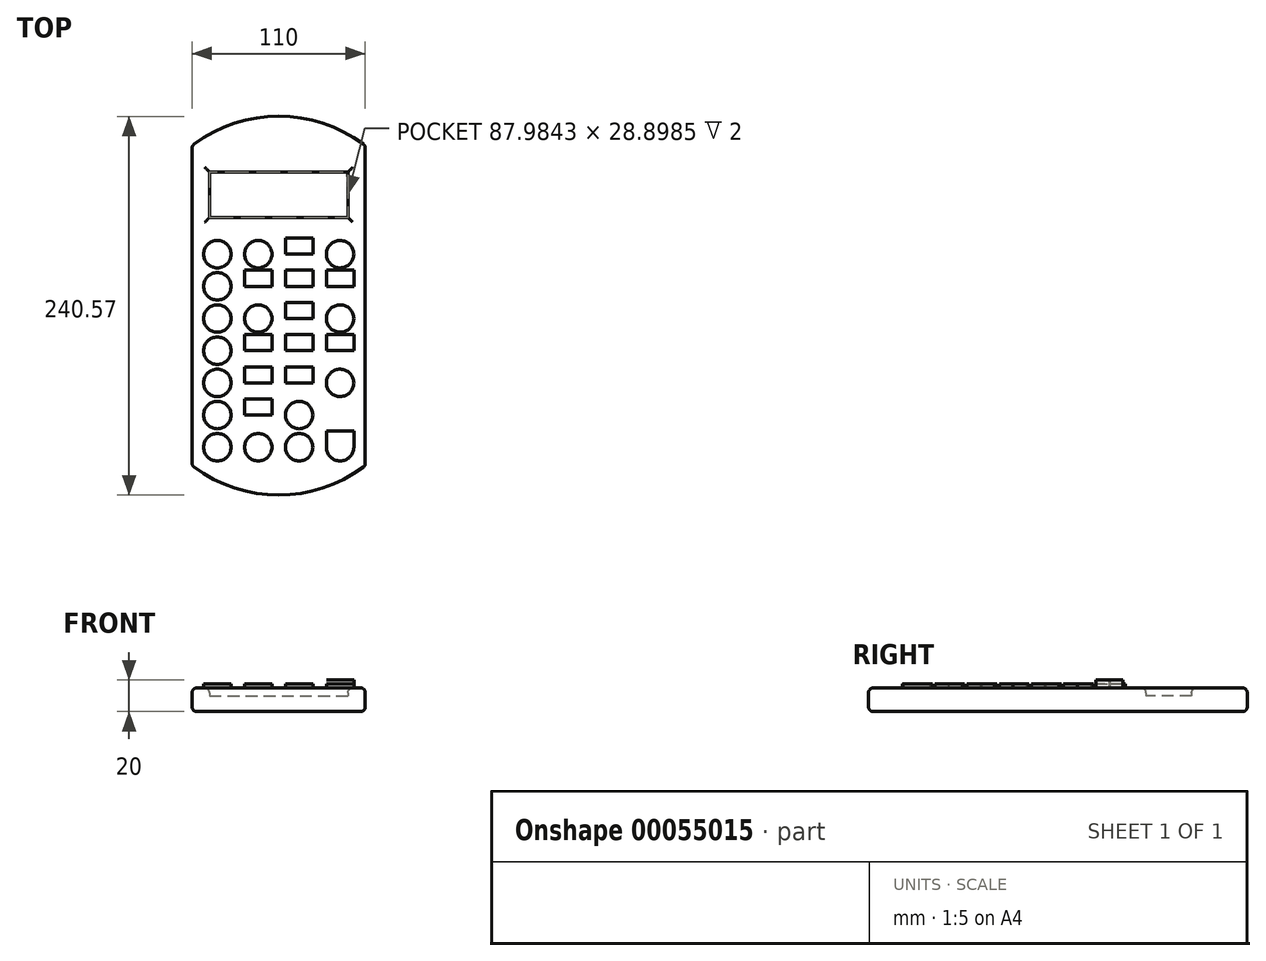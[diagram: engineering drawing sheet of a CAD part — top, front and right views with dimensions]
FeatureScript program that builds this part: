
annotation { "Feature Type Name" : "Feature", "Feature Type Description" : "" }
export const myFeature = defineFeature(function(context is Context, id is Id, definition is map)
    precondition{}
    {
        {
            var Q0;
            Q0=qCreatedBy(makeId("Top.planeOp"),FACE);
            var sketch = newSketch(context, id + "F0", { "sketchPlane" : qUnion([Q0])});
            skLineSegment(sketch, "E0.left", {"start": v(-37.1, 78.15) * mm, "end": v(-37.1, -125.06) * mm});
            skLineSegment(sketch, "E0.right", {"start": v(72.9, 78.15) * mm, "end": v(72.9, -125.06) * mm});
            skLineSegment(sketch, "E1", {"start": v(-37.1, -125.06) * mm, "end": v(72.9, -125.06) * mm});
            skPoint(sketch, "E2.endSnap0", {"position": v(17.9, -125.06) * mm});
            skArc(sketch, "E3", {"start": v(-37.1, -125.06) * mm, "mid": v(17.9, -143.74) * mm, "end": v(72.9, -125.06) * mm});
            skPoint(sketch, "E2.end.orphan", {"position": v(17.9, -16.69) * mm});
            skLineSegment(sketch, "E4", {"start": v(17.9, -125.06) * mm, "end": v(17.9, -143.74) * mm});
            skLineSegment(sketch, "E5", {"start": v(17.9, 96.83) * mm, "end": v(17.9, 78.15) * mm});
            skArc(sketch, "E6", {"start": v(72.9, 78.15) * mm, "mid": v(17.9, 96.83) * mm, "end": v(-37.1, 78.15) * mm});
            skLineSegment(sketch, "E7.rect.bottom", {"start": v(-26.1, 61.47) * mm, "end": v(61.9, 61.47) * mm});
            skLineSegment(sketch, "E7.rect.top", {"start": v(-26.1, 32.57) * mm, "end": v(61.9, 32.57) * mm});
            skLineSegment(sketch, "E7.rect.left", {"start": v(-26.1, 61.47) * mm, "end": v(-26.1, 32.57) * mm});
            skLineSegment(sketch, "E7.rect.right", {"start": v(61.9, 61.47) * mm, "end": v(61.9, 32.57) * mm});
            skPoint(sketch, "E7.rect.middle", {"position": v(17.9, 47.02) * mm});
            skPoint(sketch, "E8.orphan", {"position": v(-37.1, 96.83) * mm});
            skPoint(sketch, "E9.orphan", {"position": v(72.9, 96.83) * mm});
            skSolve(sketch);
        }
        {
            var Q0;
            {var subQ4=sQuery(id+"F0.wireOp",EDGE,"E0.left");Q0=makeQuery(id+"F0.imprint","IMPRINT",FACE,{"disambiguationData":[TD([[makeQuery(id+"F0.imprint","IMPRINT",EDGE,{"derivedFrom":subQ4}),1.0]])]});}
            var Q1;
            {var subQ3=sQuery(id+"F0.wireOp",EDGE,"E4");Q1=makeQuery(id+"F0.imprint","IMPRINT",FACE,{"disambiguationData":[TD([[makeQuery(id+"F0.imprint","IMPRINT",EDGE,{"derivedFrom":subQ3}),-1.0]])]});}
            var Q2;
            {var subQ3=sQuery(id+"F0.wireOp",EDGE,"E4");Q2=makeQuery(id+"F0.imprint","IMPRINT",FACE,{"disambiguationData":[TD([[makeQuery(id+"F0.imprint","IMPRINT",EDGE,{"derivedFrom":subQ3}),1.0]])]});}
            extrude(context, id + "F1", {"entities" : qUnion([Q0, Q1, Q2]), "depth" : 15 * mm});
        }
        {
            var Q0;
            Q0=makeQuery(id+"F0.imprint","IMPRINT",FACE,{"disambiguationData":[TD([[makeQuery(id+"F0.imprint","IMPRINT",EDGE,{"derivedFrom":sQuery(id+"F0.wireOp",EDGE,"E7.rect.bottom")}),-1.0]])]});
            extrude(context, id + "F2", {"entities" : qUnion([Q0]), "operationType" : NewBodyOperationType.ADD, "depth" : 10 * mm});
        }
        {
            var Q0;
            Q0=makeQuery(id+"F1.opExtrude","SWEPT_FACE",FACE,{"disambiguationData":[OSD([sQuery(id+"F0.wireOp",EDGE,"E3")])]});
            var Q1;
            Q1=makeQuery(id+"F1.opExtrude","SWEPT_FACE",FACE,{"disambiguationData":[OSD([sQuery(id+"F0.wireOp",EDGE,"E0.left")])]});
            var Q2;
            Q2=makeQuery(id+"F1.opExtrude","CAP_FACE",FACE,{"disambiguationData":[OSD([sQuery(id+"F0.wireOp",EDGE,"E0.left"),sQuery(id+"F0.wireOp",EDGE,"E0.right"),sQuery(id+"F0.wireOp",EDGE,"E3"),sQuery(id+"F0.wireOp",EDGE,"E6"),sQuery(id+"F0.wireOp",EDGE,"E7.rect.bottom"),sQuery(id+"F0.wireOp",EDGE,"E7.rect.top"),sQuery(id+"F0.wireOp",EDGE,"E7.rect.left"),sQuery(id+"F0.wireOp",EDGE,"E7.rect.right")])],"isStart":false});
            var Q3;
            Q3=makeQuery(id+"F1.opExtrude","SWEPT_FACE",FACE,{"disambiguationData":[OSD([sQuery(id+"F0.wireOp",EDGE,"E0.right")])]});
            var Q4;
            Q4=makeQuery(id+"F1.opExtrude","SWEPT_FACE",FACE,{"disambiguationData":[OSD([sQuery(id+"F0.wireOp",EDGE,"E6")])]});
            var Q5;
            {var subQ0=sQuery(id+"F0.wireOp",EDGE,"E7.rect.right");var subQ1=sQuery(id+"F0.wireOp",EDGE,"E7.rect.left");var subQ2=sQuery(id+"F0.wireOp",EDGE,"E7.rect.top");var subQ3=sQuery(id+"F0.wireOp",EDGE,"E7.rect.bottom");Q5=makeQuery(id+"F2.boolean.opBoolean","MERGE",FACE,{"derivedFrom":[makeQuery(id+"F1.opExtrude","CAP_FACE",FACE,{"disambiguationData":[OSD([sQuery(id+"F0.wireOp",EDGE,"E0.left"),sQuery(id+"F0.wireOp",EDGE,"E0.right"),sQuery(id+"F0.wireOp",EDGE,"E3"),sQuery(id+"F0.wireOp",EDGE,"E6"),subQ3,subQ2,subQ1,subQ0])],"isStart":true}),makeQuery(id+"F2.opExtrude","CAP_FACE",FACE,{"disambiguationData":[OSD([subQ3,subQ2,subQ1,subQ0])],"isStart":true})]});}
            fillet(context, id + "F3", {"entities" : qUnion([Q0, Q1, Q2, Q3, Q4, Q5]), "radius" : 3 * mm, "tangentPropagation" : true, "allowEdgeOverflow" : false});
        }
        {
            var Q0;
            Q0=makeQuery(id+"F1.opExtrude","CAP_FACE",FACE,{"disambiguationData":[OSD([sQuery(id+"F0.wireOp",EDGE,"E0.left"),sQuery(id+"F0.wireOp",EDGE,"E0.right"),sQuery(id+"F0.wireOp",EDGE,"E3"),sQuery(id+"F0.wireOp",EDGE,"E6"),sQuery(id+"F0.wireOp",EDGE,"E7.rect.bottom"),sQuery(id+"F0.wireOp",EDGE,"E7.rect.top"),sQuery(id+"F0.wireOp",EDGE,"E7.rect.left"),sQuery(id+"F0.wireOp",EDGE,"E7.rect.right")])],"isStart":false});
            var sketch = newSketch(context, id + "F4", { "sketchPlane" : qUnion([Q0])});
            skLineSegment(sketch, "E10", {"start": v(69.9, -103.13) * mm, "end": v(-34.1, -103.13) * mm});
            skLineSegment(sketch, "E11", {"start": v(69.9, -103.13) * mm, "end": v(17.9, -103.13) * mm});
            skLineSegment(sketch, "E12", {"start": v(17.9, -103.13) * mm, "end": v(43.9, -103.13) * mm});
            skLineSegment(sketch, "E13", {"start": v(43.9, -136.78) * mm, "end": v(43.9, 29.57) * mm});
            skLineSegment(sketch, "E14", {"start": v(17.9, 29.57) * mm, "end": v(17.9, -140.74) * mm});
            skLineSegment(sketch, "E15", {"start": v(17.9, -103.13) * mm, "end": v(-34.1, -103.13) * mm});
            skLineSegment(sketch, "E16", {"start": v(-8.1, -103.13) * mm, "end": v(-34.1, -103.13) * mm});
            skLineSegment(sketch, "E17", {"start": v(-8.1, -136.78) * mm, "end": v(-8.1, 29.57) * mm});
            skLineSegment(sketch, "E18", {"start": v(-34.1, -123.57) * mm, "end": v(69.9, -123.57) * mm});
            skLineSegment(sketch, "E19", {"start": v(-8.36, 29.57) * mm, "end": v(-8.36, 19.49) * mm});
            skPoint(sketch, "E20.start.orphan", {"position": v(-53.34, -40.82) * mm});
            skPoint(sketch, "E21.orphan", {"position": v(-79.34, -7.17) * mm});
            skPoint(sketch, "E22.end.orphan", {"position": v(-53.34, -7.17) * mm});
            skPoint(sketch, "E23.orphan", {"position": v(-27.34, -7.17) * mm});
            skPoint(sketch, "E24.start.orphan", {"position": v(-1.34, -40.82) * mm});
            skPoint(sketch, "E25.start.orphan", {"position": v(24.66, -7.17) * mm});
            skPoint(sketch, "E26.end.orphan", {"position": v(-1.34, -7.17) * mm});
            skLineSegment(sketch, "E27", {"start": v(-34.1, 19.49) * mm, "end": v(69.9, 19.49) * mm});
            skLineSegment(sketch, "E28", {"start": v(-34.1, -82.7) * mm, "end": v(69.9, -82.7) * mm});
            skLineSegment(sketch, "E29", {"start": v(-34.1, -62.26) * mm, "end": v(69.9, -62.26) * mm});
            skLineSegment(sketch, "E30", {"start": v(-34.1, -41.82) * mm, "end": v(69.9, -41.82) * mm});
            skLineSegment(sketch, "E31", {"start": v(-34.1, -21.38) * mm, "end": v(69.9, -21.38) * mm});
            skLineSegment(sketch, "E32", {"start": v(-34.1, -0.95) * mm, "end": v(69.9, -0.95) * mm});
            skLineSegment(sketch, "E33.bottom", {"start": v(65.6, -113.35) * mm, "end": v(48.2, -113.35) * mm});
            skLineSegment(sketch, "E33.top", {"start": v(65.6, -84.18) * mm, "end": v(48.2, -84.18) * mm});
            skLineSegment(sketch, "E33.left", {"start": v(65.6, -113.35) * mm, "end": v(65.6, -84.18) * mm});
            skLineSegment(sketch, "E33.right", {"start": v(48.2, -113.35) * mm, "end": v(48.2, -84.18) * mm});
            skLineSegment(sketch, "E34", {"start": v(48.2, -84.18) * mm, "end": v(48.2, -103.13) * mm});
            skLineSegment(sketch, "E35", {"start": v(48.2, -103.13) * mm, "end": v(48.2, -93.66) * mm});
            skArc(sketch, "E36", {"start": v(65.6, -93.66) * mm, "mid": v(56.9, -84.18) * mm, "end": v(48.2, -93.66) * mm});
            skLineSegment(sketch, "E37", {"start": v(43.9, -82.7) * mm, "end": v(43.9, -103.13) * mm});
            skLineSegment(sketch, "E38", {"start": v(43.9, -92.91) * mm, "end": v(56.9, -92.91) * mm});
            skLineSegment(sketch, "E39", {"start": v(43.9, -103.13) * mm, "end": v(43.9, -123.57) * mm});
            skLineSegment(sketch, "E40", {"start": v(43.9, -123.57) * mm, "end": v(43.9, -113.35) * mm});
            skLineSegment(sketch, "E41", {"start": v(43.9, -113.35) * mm, "end": v(56.9, -113.35) * mm});
            skPoint(sketch, "E41.endSnap0", {"position": v(56.9, -113.35) * mm});
            skArc(sketch, "E42", {"start": v(48.2, -113.35) * mm, "mid": v(56.9, -122.04) * mm, "end": v(65.6, -113.35) * mm});
            skLineSegment(sketch, "E43", {"start": v(43.9, -62.26) * mm, "end": v(43.9, -82.7) * mm});
            skLineSegment(sketch, "E44", {"start": v(43.9, -72.47) * mm, "end": v(69.9, -72.47) * mm});
            skLineSegment(sketch, "E45", {"start": v(65.6, -84.18) * mm, "end": v(65.6, -62.26) * mm});
            skLineSegment(sketch, "E46", {"start": v(48.2, -84.18) * mm, "end": v(48.2, -62.26) * mm});
            skCircle(sketch, "E47", {"center": v(56.9, -72.47) * mm, "radius": 8.7 * mm});
            skLineSegment(sketch, "E48", {"start": v(48.2, -62.26) * mm, "end": v(48.2, 19.49) * mm});
            skLineSegment(sketch, "E49", {"start": v(65.6, -62.26) * mm, "end": v(65.6, 19.49) * mm});
            skLineSegment(sketch, "E50", {"start": v(43.9, -62.26) * mm, "end": v(43.9, -41.82) * mm});
            skLineSegment(sketch, "E51", {"start": v(43.9, -41.82) * mm, "end": v(43.9, -52.04) * mm});
            skLineSegment(sketch, "E52", {"start": v(43.9, -52.04) * mm, "end": v(69.9, -52.04) * mm});
            skLineSegment(sketch, "E53", {"start": v(43.9, -21.38) * mm, "end": v(43.9, -41.82) * mm});
            skLineSegment(sketch, "E54", {"start": v(43.9, -31.6) * mm, "end": v(69.9, -31.6) * mm});
            skLineSegment(sketch, "E55", {"start": v(43.9, -0.95) * mm, "end": v(43.9, -21.38) * mm});
            skLineSegment(sketch, "E56", {"start": v(43.9, -11.16) * mm, "end": v(69.9, -11.16) * mm});
            skLineSegment(sketch, "E57", {"start": v(43.9, -0.95) * mm, "end": v(43.9, 19.49) * mm});
            skLineSegment(sketch, "E58", {"start": v(43.9, 19.49) * mm, "end": v(43.9, 9.27) * mm});
            skLineSegment(sketch, "E59", {"start": v(43.9, 9.27) * mm, "end": v(69.9, 9.27) * mm});
            skCircle(sketch, "E60", {"center": v(56.9, 9.27) * mm, "radius": 8.7 * mm});
            skCircle(sketch, "E61", {"center": v(56.9, -11.16) * mm, "radius": 8.7 * mm});
            skCircle(sketch, "E62", {"center": v(56.9, -31.6) * mm, "radius": 8.7 * mm});
            skCircle(sketch, "E63", {"center": v(56.9, -52.04) * mm, "radius": 8.7 * mm});
            skLineSegment(sketch, "E64", {"start": v(22.2, -123.57) * mm, "end": v(22.2, 19.49) * mm});
            skLineSegment(sketch, "E65", {"start": v(39.6, -123.57) * mm, "end": v(39.6, 19.49) * mm});
            skLineSegment(sketch, "E66", {"start": v(17.9, -103.13) * mm, "end": v(17.9, -123.57) * mm});
            skLineSegment(sketch, "E67", {"start": v(17.9, -123.57) * mm, "end": v(17.9, -113.35) * mm});
            skLineSegment(sketch, "E68", {"start": v(17.9, -103.13) * mm, "end": v(17.9, -82.7) * mm});
            skLineSegment(sketch, "E69", {"start": v(17.9, -113.35) * mm, "end": v(43.9, -113.35) * mm});
            skCircle(sketch, "E70", {"center": v(30.9, -113.35) * mm, "radius": 8.7 * mm});
            skLineSegment(sketch, "E71", {"start": v(30.9, -113.35) * mm, "end": v(30.9, 19.49) * mm});
            skLineSegment(sketch, "E72", {"start": v(-8.1, -103.13) * mm, "end": v(-8.1, -123.57) * mm});
            skLineSegment(sketch, "E73", {"start": v(-8.1, -123.57) * mm, "end": v(-8.1, -113.35) * mm});
            skLineSegment(sketch, "E74", {"start": v(-8.1, -113.35) * mm, "end": v(17.9, -113.35) * mm});
            skLineSegment(sketch, "E75", {"start": v(-34.1, -113.35) * mm, "end": v(-8.1, -113.35) * mm});
            skLineSegment(sketch, "E76", {"start": v(4.9, -123.57) * mm, "end": v(4.9, 19.49) * mm});
            skPoint(sketch, "E76.startSnap0", {"position": v(4.9, -113.35) * mm});
            skLineSegment(sketch, "E77", {"start": v(43.9, 9.27) * mm, "end": v(-34.1, 9.27) * mm});
            skLineSegment(sketch, "E78", {"start": v(43.9, -11.16) * mm, "end": v(-34.1, -11.16) * mm});
            skLineSegment(sketch, "E79", {"start": v(43.9, -31.6) * mm, "end": v(-34.1, -31.6) * mm});
            skLineSegment(sketch, "E80", {"start": v(43.9, -52.04) * mm, "end": v(-34.1, -52.04) * mm});
            skLineSegment(sketch, "E81", {"start": v(43.9, -72.47) * mm, "end": v(-34.1, -72.47) * mm});
            skLineSegment(sketch, "E82", {"start": v(43.9, -92.91) * mm, "end": v(-34.1, -92.91) * mm});
            skLineSegment(sketch, "E83", {"start": v(-21.1, -113.35) * mm, "end": v(-21.1, 19.49) * mm});
            skCircle(sketch, "E84", {"center": v(30.9, -92.91) * mm, "radius": 8.7 * mm});
            skCircle(sketch, "E85", {"center": v(30.9, -72.47) * mm, "radius": 8.7 * mm});
            skCircle(sketch, "E86", {"center": v(30.9, -52.04) * mm, "radius": 8.7 * mm});
            skCircle(sketch, "E87", {"center": v(30.9, -31.6) * mm, "radius": 8.7 * mm});
            skCircle(sketch, "E88", {"center": v(30.9, -11.16) * mm, "radius": 8.7 * mm});
            skCircle(sketch, "E89", {"center": v(30.9, 9.27) * mm, "radius": 8.7 * mm});
            skLineSegment(sketch, "E90", {"start": v(-8.1, 14.54) * mm, "end": v(-3.8, 14.54) * mm});
            skLineSegment(sketch, "E91", {"start": v(17.9, 14.54) * mm, "end": v(13.6, 14.54) * mm});
            skLineSegment(sketch, "E92", {"start": v(-34.1, 15.12) * mm, "end": v(-29.8, 15.12) * mm});
            skLineSegment(sketch, "E93", {"start": v(-8.1, 14.54) * mm, "end": v(-12.4, 14.54) * mm});
            skLineSegment(sketch, "E94", {"start": v(-29.8, 19.49) * mm, "end": v(-29.8, -113.35) * mm});
            skLineSegment(sketch, "E95", {"start": v(-12.4, 14.54) * mm, "end": v(-12.4, 19.49) * mm});
            skLineSegment(sketch, "E96", {"start": v(-12.4, 19.49) * mm, "end": v(-12.4, -113.35) * mm});
            skLineSegment(sketch, "E97", {"start": v(-3.8, 19.49) * mm, "end": v(-3.8, -113.35) * mm});
            skLineSegment(sketch, "E98", {"start": v(13.6, 19.49) * mm, "end": v(13.6, -113.35) * mm});
            skCircle(sketch, "E99", {"center": v(4.9, 9.27) * mm, "radius": 8.7 * mm});
            skCircle(sketch, "E100", {"center": v(4.9, -11.16) * mm, "radius": 8.7 * mm});
            skCircle(sketch, "E101", {"center": v(4.9, -31.6) * mm, "radius": 8.7 * mm});
            skCircle(sketch, "E102", {"center": v(4.9, -52.04) * mm, "radius": 8.7 * mm});
            skCircle(sketch, "E103", {"center": v(4.9, -72.47) * mm, "radius": 8.7 * mm});
            skCircle(sketch, "E104", {"center": v(4.9, -92.91) * mm, "radius": 8.7 * mm});
            skCircle(sketch, "E105", {"center": v(4.9, -113.35) * mm, "radius": 8.7 * mm});
            skCircle(sketch, "E106", {"center": v(-21.1, -113.35) * mm, "radius": 8.7 * mm});
            skCircle(sketch, "E107", {"center": v(-21.1, -92.91) * mm, "radius": 8.7 * mm});
            skCircle(sketch, "E108", {"center": v(-21.1, -72.47) * mm, "radius": 8.7 * mm});
            skCircle(sketch, "E109", {"center": v(-21.1, -52.04) * mm, "radius": 8.7 * mm});
            skCircle(sketch, "E110", {"center": v(-21.1, -31.6) * mm, "radius": 8.7 * mm});
            skCircle(sketch, "E111", {"center": v(-21.1, -11.16) * mm, "radius": 8.7 * mm});
            skCircle(sketch, "E112", {"center": v(-21.1, 9.27) * mm, "radius": 8.7 * mm});
            skSolve(sketch);
        }
        {
            var Q0;
            {var subQ7=sQuery(id+"F4.wireOp",EDGE,"E35");Q0=makeQuery(id+"F4.imprint","IMPRINT",FACE,{"disambiguationData":[TD([[makeQuery(id+"F4.imprint","IMPRINT",EDGE,{"derivedFrom":subQ7}),-1.0]])]});}
            var Q1;
            {var subQ3=sQuery(id+"F4.wireOp",EDGE,"E33.bottom");Q1=makeQuery(id+"F4.imprint","IMPRINT",FACE,{"disambiguationData":[TD([[makeQuery(id+"F4.imprint","IMPRINT",EDGE,{"derivedFrom":subQ3}),-1.0]])]});}
            var Q2;
            {var subQ0=sQuery(id+"F4.wireOp",EDGE,"E33.bottom");Q2=makeQuery(id+"F4.imprint","IMPRINT",FACE,{"disambiguationData":[TD([[makeQuery(id+"F4.imprint","IMPRINT",EDGE,{"derivedFrom":subQ0}),1.0]])]});}
            extrude(context, id + "F5", {"entities" : qUnion([Q0, Q1, Q2]), "operationType" : NewBodyOperationType.ADD, "depth" : 2.5 * mm});
        }
        {
            var Q0;
            {var subQ0=sQuery(id+"F4.wireOp",EDGE,"E46");var subQ1=sQuery(id+"F4.wireOp",EDGE,"E44");var subQ2=makeQuery(id+"F4.imprint","INTERSECT",VERTEX,{"derivedFrom":[subQ1,subQ0]});Q0=makeQuery(id+"F4.imprint","IMPRINT",FACE,{"disambiguationData":[TD([[makeQuery(id+"F4.imprint","IMPRINT",EDGE,{"disambiguationData":[TD([[subQ2,-1.0]])],"derivedFrom":subQ0}),-1.0]])]});}
            var Q1;
            {var subQ0=sQuery(id+"F4.wireOp",EDGE,"E46");var subQ1=sQuery(id+"F4.wireOp",EDGE,"E44");var subQ2=makeQuery(id+"F4.imprint","INTERSECT",VERTEX,{"derivedFrom":[subQ1,subQ0]});Q1=makeQuery(id+"F4.imprint","IMPRINT",FACE,{"disambiguationData":[TD([[makeQuery(id+"F4.imprint","IMPRINT",EDGE,{"disambiguationData":[TD([[subQ2,1.0]])],"derivedFrom":subQ0}),-1.0]])]});}
            extrude(context, id + "F6", {"entities" : qUnion([Q0, Q1]), "operationType" : NewBodyOperationType.ADD, "depth" : 2.5 * mm});
        }
        {
            var Q0;
            {var subQ0=sQuery(id+"F4.wireOp",EDGE,"E59");var subQ1=sQuery(id+"F4.wireOp",EDGE,"E48");var subQ2=makeQuery(id+"F4.imprint","INTERSECT",VERTEX,{"derivedFrom":[subQ1,subQ0]});Q0=makeQuery(id+"F4.imprint","IMPRINT",FACE,{"disambiguationData":[TD([[makeQuery(id+"F4.imprint","IMPRINT",EDGE,{"disambiguationData":[TD([[subQ2,-1.0]])],"derivedFrom":subQ1}),-1.0]])]});}
            var Q1;
            {var subQ0=sQuery(id+"F4.wireOp",EDGE,"E60");var subQ1=sQuery(id+"F4.wireOp",EDGE,"E48");var subQ2=makeQuery(id+"F4.imprint","INTERSECT",VERTEX,{"disambiguationData":[OD(0.0)],"derivedFrom":[subQ1,subQ0]});Q1=makeQuery(id+"F4.imprint","IMPRINT",FACE,{"disambiguationData":[TD([[makeQuery(id+"F4.imprint","IMPRINT",EDGE,{"disambiguationData":[TD([[subQ2,-1.0]])],"derivedFrom":subQ1}),-1.0]])]});}
            var Q2;
            {var subQ0=sQuery(id+"F4.wireOp",EDGE,"E56");var subQ1=sQuery(id+"F4.wireOp",EDGE,"E48");var subQ2=makeQuery(id+"F4.imprint","INTERSECT",VERTEX,{"derivedFrom":[subQ1,subQ0]});Q2=makeQuery(id+"F4.imprint","IMPRINT",FACE,{"disambiguationData":[TD([[makeQuery(id+"F4.imprint","IMPRINT",EDGE,{"disambiguationData":[TD([[subQ2,-1.0]])],"derivedFrom":subQ1}),-1.0]])]});}
            var Q3;
            {var subQ0=sQuery(id+"F4.wireOp",EDGE,"E61");var subQ1=sQuery(id+"F4.wireOp",EDGE,"E48");var subQ2=makeQuery(id+"F4.imprint","INTERSECT",VERTEX,{"disambiguationData":[OD(0.0)],"derivedFrom":[subQ1,subQ0]});Q3=makeQuery(id+"F4.imprint","IMPRINT",FACE,{"disambiguationData":[TD([[makeQuery(id+"F4.imprint","IMPRINT",EDGE,{"disambiguationData":[TD([[subQ2,-1.0]])],"derivedFrom":subQ1}),-1.0]])]});}
            var Q4;
            {var subQ0=sQuery(id+"F4.wireOp",EDGE,"E54");var subQ1=sQuery(id+"F4.wireOp",EDGE,"E48");var subQ2=makeQuery(id+"F4.imprint","INTERSECT",VERTEX,{"derivedFrom":[subQ1,subQ0]});Q4=makeQuery(id+"F4.imprint","IMPRINT",FACE,{"disambiguationData":[TD([[makeQuery(id+"F4.imprint","IMPRINT",EDGE,{"disambiguationData":[TD([[subQ2,-1.0]])],"derivedFrom":subQ1}),-1.0]])]});}
            var Q5;
            {var subQ0=sQuery(id+"F4.wireOp",EDGE,"E62");var subQ1=sQuery(id+"F4.wireOp",EDGE,"E48");var subQ2=makeQuery(id+"F4.imprint","INTERSECT",VERTEX,{"disambiguationData":[OD(0.0)],"derivedFrom":[subQ1,subQ0]});Q5=makeQuery(id+"F4.imprint","IMPRINT",FACE,{"disambiguationData":[TD([[makeQuery(id+"F4.imprint","IMPRINT",EDGE,{"disambiguationData":[TD([[subQ2,-1.0]])],"derivedFrom":subQ1}),-1.0]])]});}
            var Q6;
            {var subQ0=sQuery(id+"F4.wireOp",EDGE,"E52");var subQ1=sQuery(id+"F4.wireOp",EDGE,"E48");var subQ2=makeQuery(id+"F4.imprint","INTERSECT",VERTEX,{"derivedFrom":[subQ1,subQ0]});Q6=makeQuery(id+"F4.imprint","IMPRINT",FACE,{"disambiguationData":[TD([[makeQuery(id+"F4.imprint","IMPRINT",EDGE,{"disambiguationData":[TD([[subQ2,-1.0]])],"derivedFrom":subQ1}),-1.0]])]});}
            var Q7;
            {var subQ0=sQuery(id+"F4.wireOp",EDGE,"E63");var subQ1=sQuery(id+"F4.wireOp",EDGE,"E48");var subQ2=makeQuery(id+"F4.imprint","INTERSECT",VERTEX,{"disambiguationData":[OD(0.0)],"derivedFrom":[subQ1,subQ0]});Q7=makeQuery(id+"F4.imprint","IMPRINT",FACE,{"disambiguationData":[TD([[makeQuery(id+"F4.imprint","IMPRINT",EDGE,{"disambiguationData":[TD([[subQ2,-1.0]])],"derivedFrom":subQ1}),-1.0]])]});}
            extrude(context, id + "F7", {"entities" : qUnion([Q0, Q1, Q2, Q3, Q4, Q5, Q6, Q7]), "operationType" : NewBodyOperationType.ADD, "depth" : 2.5 * mm});
        }
        {
            var Q0;
            {var subQ0=sQuery(id+"F4.wireOp",EDGE,"E70");var subQ1=sQuery(id+"F4.wireOp",EDGE,"E69");var subQ2=makeQuery(id+"F4.imprint","INTERSECT",VERTEX,{"derivedFrom":[sQuery(id+"F4.wireOp",EDGE,"E64"),subQ1,subQ0]});Q0=makeQuery(id+"F4.imprint","IMPRINT",FACE,{"disambiguationData":[TD([[makeQuery(id+"F4.imprint","IMPRINT",EDGE,{"disambiguationData":[TD([[subQ2,-1.0]])],"derivedFrom":subQ1}),1.0]])]});}
            var Q1;
            {var subQ0=sQuery(id+"F4.wireOp",EDGE,"E70");var subQ1=sQuery(id+"F4.wireOp",EDGE,"E69");var subQ2=makeQuery(id+"F4.imprint","INTERSECT",VERTEX,{"derivedFrom":[sQuery(id+"F4.wireOp",EDGE,"E64"),subQ1,subQ0]});Q1=makeQuery(id+"F4.imprint","IMPRINT",FACE,{"disambiguationData":[TD([[makeQuery(id+"F4.imprint","IMPRINT",EDGE,{"disambiguationData":[TD([[subQ2,-1.0]])],"derivedFrom":subQ1}),-1.0]])]});}
            extrude(context, id + "F8", {"entities" : qUnion([Q0, Q1]), "operationType" : NewBodyOperationType.ADD, "depth" : 2.5 * mm});
        }
        {
            var Q0;
            {var subQ0=sQuery(id+"F4.wireOp",EDGE,"E71");var subQ1=sQuery(id+"F4.wireOp",EDGE,"E69");var subQ2=makeQuery(id+"F4.imprint","INTERSECT",VERTEX,{"derivedFrom":[subQ1,subQ0]});Q0=makeQuery(id+"F4.imprint","IMPRINT",FACE,{"disambiguationData":[TD([[makeQuery(id+"F4.imprint","IMPRINT",EDGE,{"disambiguationData":[TD([[subQ2,-1.0]])],"derivedFrom":subQ0}),-1.0]])]});}
            extrude(context, id + "F9", {"entities" : qUnion([Q0]), "operationType" : NewBodyOperationType.ADD, "depth" : 2.5 * mm});
        }
        {
            var Q0;
            {var subQ0=sQuery(id+"F4.wireOp",EDGE,"E84");var subQ1=sQuery(id+"F4.wireOp",EDGE,"E71");var subQ2=makeQuery(id+"F4.imprint","INTERSECT",VERTEX,{"disambiguationData":[OD(0.0)],"derivedFrom":[subQ1,subQ0]});Q0=makeQuery(id+"F4.imprint","IMPRINT",FACE,{"disambiguationData":[TD([[makeQuery(id+"F4.imprint","IMPRINT",EDGE,{"disambiguationData":[TD([[subQ2,-1.0]])],"derivedFrom":subQ1}),-1.0]])]});}
            var Q1;
            {var subQ0=sQuery(id+"F4.wireOp",EDGE,"E84");var subQ1=sQuery(id+"F4.wireOp",EDGE,"E71");var subQ2=makeQuery(id+"F4.imprint","INTERSECT",VERTEX,{"disambiguationData":[OD(0.0)],"derivedFrom":[subQ1,subQ0]});Q1=makeQuery(id+"F4.imprint","IMPRINT",FACE,{"disambiguationData":[TD([[makeQuery(id+"F4.imprint","IMPRINT",EDGE,{"disambiguationData":[TD([[subQ2,-1.0]])],"derivedFrom":subQ1}),1.0]])]});}
            var Q2;
            {var subQ0=sQuery(id+"F4.wireOp",EDGE,"E82");var subQ1=sQuery(id+"F4.wireOp",EDGE,"E71");var subQ2=makeQuery(id+"F4.imprint","INTERSECT",VERTEX,{"derivedFrom":[subQ1,subQ0]});Q2=makeQuery(id+"F4.imprint","IMPRINT",FACE,{"disambiguationData":[TD([[makeQuery(id+"F4.imprint","IMPRINT",EDGE,{"disambiguationData":[TD([[subQ2,-1.0]])],"derivedFrom":subQ1}),1.0]])]});}
            var Q3;
            {var subQ0=sQuery(id+"F4.wireOp",EDGE,"E82");var subQ1=sQuery(id+"F4.wireOp",EDGE,"E71");var subQ2=makeQuery(id+"F4.imprint","INTERSECT",VERTEX,{"derivedFrom":[subQ1,subQ0]});Q3=makeQuery(id+"F4.imprint","IMPRINT",FACE,{"disambiguationData":[TD([[makeQuery(id+"F4.imprint","IMPRINT",EDGE,{"disambiguationData":[TD([[subQ2,-1.0]])],"derivedFrom":subQ1}),-1.0]])]});}
            var Q4;
            {var subQ0=sQuery(id+"F4.wireOp",EDGE,"E85");var subQ1=sQuery(id+"F4.wireOp",EDGE,"E71");var subQ2=makeQuery(id+"F4.imprint","INTERSECT",VERTEX,{"disambiguationData":[OD(0.0)],"derivedFrom":[subQ1,subQ0]});Q4=makeQuery(id+"F4.imprint","IMPRINT",FACE,{"disambiguationData":[TD([[makeQuery(id+"F4.imprint","IMPRINT",EDGE,{"disambiguationData":[TD([[subQ2,-1.0]])],"derivedFrom":subQ1}),-1.0]])]});}
            var Q5;
            {var subQ0=sQuery(id+"F4.wireOp",EDGE,"E85");var subQ1=sQuery(id+"F4.wireOp",EDGE,"E71");var subQ2=makeQuery(id+"F4.imprint","INTERSECT",VERTEX,{"disambiguationData":[OD(0.0)],"derivedFrom":[subQ1,subQ0]});Q5=makeQuery(id+"F4.imprint","IMPRINT",FACE,{"disambiguationData":[TD([[makeQuery(id+"F4.imprint","IMPRINT",EDGE,{"disambiguationData":[TD([[subQ2,-1.0]])],"derivedFrom":subQ1}),1.0]])]});}
            var Q6;
            {var subQ0=sQuery(id+"F4.wireOp",EDGE,"E81");var subQ1=sQuery(id+"F4.wireOp",EDGE,"E71");var subQ2=makeQuery(id+"F4.imprint","INTERSECT",VERTEX,{"derivedFrom":[subQ1,subQ0]});Q6=makeQuery(id+"F4.imprint","IMPRINT",FACE,{"disambiguationData":[TD([[makeQuery(id+"F4.imprint","IMPRINT",EDGE,{"disambiguationData":[TD([[subQ2,-1.0]])],"derivedFrom":subQ1}),1.0]])]});}
            var Q7;
            {var subQ0=sQuery(id+"F4.wireOp",EDGE,"E81");var subQ1=sQuery(id+"F4.wireOp",EDGE,"E71");var subQ2=makeQuery(id+"F4.imprint","INTERSECT",VERTEX,{"derivedFrom":[subQ1,subQ0]});Q7=makeQuery(id+"F4.imprint","IMPRINT",FACE,{"disambiguationData":[TD([[makeQuery(id+"F4.imprint","IMPRINT",EDGE,{"disambiguationData":[TD([[subQ2,-1.0]])],"derivedFrom":subQ1}),-1.0]])]});}
            var Q8;
            {var subQ0=sQuery(id+"F4.wireOp",EDGE,"E80");var subQ1=sQuery(id+"F4.wireOp",EDGE,"E71");var subQ2=makeQuery(id+"F4.imprint","INTERSECT",VERTEX,{"derivedFrom":[subQ1,subQ0]});Q8=makeQuery(id+"F4.imprint","IMPRINT",FACE,{"disambiguationData":[TD([[makeQuery(id+"F4.imprint","IMPRINT",EDGE,{"disambiguationData":[TD([[subQ2,-1.0]])],"derivedFrom":subQ1}),1.0]])]});}
            var Q9;
            {var subQ0=sQuery(id+"F4.wireOp",EDGE,"E80");var subQ1=sQuery(id+"F4.wireOp",EDGE,"E71");var subQ2=makeQuery(id+"F4.imprint","INTERSECT",VERTEX,{"derivedFrom":[subQ1,subQ0]});Q9=makeQuery(id+"F4.imprint","IMPRINT",FACE,{"disambiguationData":[TD([[makeQuery(id+"F4.imprint","IMPRINT",EDGE,{"disambiguationData":[TD([[subQ2,-1.0]])],"derivedFrom":subQ1}),-1.0]])]});}
            var Q10;
            {var subQ0=sQuery(id+"F4.wireOp",EDGE,"E86");var subQ1=sQuery(id+"F4.wireOp",EDGE,"E71");var subQ2=makeQuery(id+"F4.imprint","INTERSECT",VERTEX,{"disambiguationData":[OD(0.0)],"derivedFrom":[subQ1,subQ0]});Q10=makeQuery(id+"F4.imprint","IMPRINT",FACE,{"disambiguationData":[TD([[makeQuery(id+"F4.imprint","IMPRINT",EDGE,{"disambiguationData":[TD([[subQ2,-1.0]])],"derivedFrom":subQ1}),-1.0]])]});}
            var Q11;
            {var subQ0=sQuery(id+"F4.wireOp",EDGE,"E86");var subQ1=sQuery(id+"F4.wireOp",EDGE,"E71");var subQ2=makeQuery(id+"F4.imprint","INTERSECT",VERTEX,{"disambiguationData":[OD(0.0)],"derivedFrom":[subQ1,subQ0]});Q11=makeQuery(id+"F4.imprint","IMPRINT",FACE,{"disambiguationData":[TD([[makeQuery(id+"F4.imprint","IMPRINT",EDGE,{"disambiguationData":[TD([[subQ2,-1.0]])],"derivedFrom":subQ1}),1.0]])]});}
            var Q12;
            {var subQ0=sQuery(id+"F4.wireOp",EDGE,"E87");var subQ1=sQuery(id+"F4.wireOp",EDGE,"E71");var subQ2=makeQuery(id+"F4.imprint","INTERSECT",VERTEX,{"disambiguationData":[OD(0.0)],"derivedFrom":[subQ1,subQ0]});Q12=makeQuery(id+"F4.imprint","IMPRINT",FACE,{"disambiguationData":[TD([[makeQuery(id+"F4.imprint","IMPRINT",EDGE,{"disambiguationData":[TD([[subQ2,-1.0]])],"derivedFrom":subQ1}),-1.0]])]});}
            var Q13;
            {var subQ0=sQuery(id+"F4.wireOp",EDGE,"E87");var subQ1=sQuery(id+"F4.wireOp",EDGE,"E71");var subQ2=makeQuery(id+"F4.imprint","INTERSECT",VERTEX,{"disambiguationData":[OD(0.0)],"derivedFrom":[subQ1,subQ0]});Q13=makeQuery(id+"F4.imprint","IMPRINT",FACE,{"disambiguationData":[TD([[makeQuery(id+"F4.imprint","IMPRINT",EDGE,{"disambiguationData":[TD([[subQ2,-1.0]])],"derivedFrom":subQ1}),1.0]])]});}
            var Q14;
            {var subQ0=sQuery(id+"F4.wireOp",EDGE,"E79");var subQ1=sQuery(id+"F4.wireOp",EDGE,"E71");var subQ2=makeQuery(id+"F4.imprint","INTERSECT",VERTEX,{"derivedFrom":[subQ1,subQ0]});Q14=makeQuery(id+"F4.imprint","IMPRINT",FACE,{"disambiguationData":[TD([[makeQuery(id+"F4.imprint","IMPRINT",EDGE,{"disambiguationData":[TD([[subQ2,-1.0]])],"derivedFrom":subQ1}),1.0]])]});}
            var Q15;
            {var subQ0=sQuery(id+"F4.wireOp",EDGE,"E79");var subQ1=sQuery(id+"F4.wireOp",EDGE,"E71");var subQ2=makeQuery(id+"F4.imprint","INTERSECT",VERTEX,{"derivedFrom":[subQ1,subQ0]});Q15=makeQuery(id+"F4.imprint","IMPRINT",FACE,{"disambiguationData":[TD([[makeQuery(id+"F4.imprint","IMPRINT",EDGE,{"disambiguationData":[TD([[subQ2,-1.0]])],"derivedFrom":subQ1}),-1.0]])]});}
            var Q16;
            {var subQ0=sQuery(id+"F4.wireOp",EDGE,"E88");var subQ1=sQuery(id+"F4.wireOp",EDGE,"E71");var subQ2=makeQuery(id+"F4.imprint","INTERSECT",VERTEX,{"disambiguationData":[OD(0.0)],"derivedFrom":[subQ1,subQ0]});Q16=makeQuery(id+"F4.imprint","IMPRINT",FACE,{"disambiguationData":[TD([[makeQuery(id+"F4.imprint","IMPRINT",EDGE,{"disambiguationData":[TD([[subQ2,-1.0]])],"derivedFrom":subQ1}),-1.0]])]});}
            var Q17;
            {var subQ0=sQuery(id+"F4.wireOp",EDGE,"E88");var subQ1=sQuery(id+"F4.wireOp",EDGE,"E71");var subQ2=makeQuery(id+"F4.imprint","INTERSECT",VERTEX,{"disambiguationData":[OD(0.0)],"derivedFrom":[subQ1,subQ0]});Q17=makeQuery(id+"F4.imprint","IMPRINT",FACE,{"disambiguationData":[TD([[makeQuery(id+"F4.imprint","IMPRINT",EDGE,{"disambiguationData":[TD([[subQ2,-1.0]])],"derivedFrom":subQ1}),1.0]])]});}
            var Q18;
            {var subQ0=sQuery(id+"F4.wireOp",EDGE,"E78");var subQ1=sQuery(id+"F4.wireOp",EDGE,"E71");var subQ2=makeQuery(id+"F4.imprint","INTERSECT",VERTEX,{"derivedFrom":[subQ1,subQ0]});Q18=makeQuery(id+"F4.imprint","IMPRINT",FACE,{"disambiguationData":[TD([[makeQuery(id+"F4.imprint","IMPRINT",EDGE,{"disambiguationData":[TD([[subQ2,-1.0]])],"derivedFrom":subQ1}),1.0]])]});}
            var Q19;
            {var subQ0=sQuery(id+"F4.wireOp",EDGE,"E78");var subQ1=sQuery(id+"F4.wireOp",EDGE,"E71");var subQ2=makeQuery(id+"F4.imprint","INTERSECT",VERTEX,{"derivedFrom":[subQ1,subQ0]});Q19=makeQuery(id+"F4.imprint","IMPRINT",FACE,{"disambiguationData":[TD([[makeQuery(id+"F4.imprint","IMPRINT",EDGE,{"disambiguationData":[TD([[subQ2,-1.0]])],"derivedFrom":subQ1}),-1.0]])]});}
            var Q20;
            {var subQ0=sQuery(id+"F4.wireOp",EDGE,"E78");var subQ1=sQuery(id+"F4.wireOp",EDGE,"E76");var subQ2=makeQuery(id+"F4.imprint","INTERSECT",VERTEX,{"derivedFrom":[subQ1,subQ0]});Q20=makeQuery(id+"F4.imprint","IMPRINT",FACE,{"disambiguationData":[TD([[makeQuery(id+"F4.imprint","IMPRINT",EDGE,{"disambiguationData":[TD([[subQ2,-1.0]])],"derivedFrom":subQ1}),-1.0]])]});}
            var Q21;
            {var subQ0=sQuery(id+"F4.wireOp",EDGE,"E78");var subQ1=sQuery(id+"F4.wireOp",EDGE,"E76");var subQ2=makeQuery(id+"F4.imprint","INTERSECT",VERTEX,{"derivedFrom":[subQ1,subQ0]});Q21=makeQuery(id+"F4.imprint","IMPRINT",FACE,{"disambiguationData":[TD([[makeQuery(id+"F4.imprint","IMPRINT",EDGE,{"disambiguationData":[TD([[subQ2,-1.0]])],"derivedFrom":subQ1}),1.0]])]});}
            var Q22;
            {var subQ0=sQuery(id+"F4.wireOp",EDGE,"E100");var subQ1=sQuery(id+"F4.wireOp",EDGE,"E76");var subQ2=makeQuery(id+"F4.imprint","INTERSECT",VERTEX,{"disambiguationData":[OD(0.0)],"derivedFrom":[subQ1,subQ0]});Q22=makeQuery(id+"F4.imprint","IMPRINT",FACE,{"disambiguationData":[TD([[makeQuery(id+"F4.imprint","IMPRINT",EDGE,{"disambiguationData":[TD([[subQ2,-1.0]])],"derivedFrom":subQ1}),1.0]])]});}
            var Q23;
            {var subQ0=sQuery(id+"F4.wireOp",EDGE,"E100");var subQ1=sQuery(id+"F4.wireOp",EDGE,"E76");var subQ2=makeQuery(id+"F4.imprint","INTERSECT",VERTEX,{"disambiguationData":[OD(0.0)],"derivedFrom":[subQ1,subQ0]});Q23=makeQuery(id+"F4.imprint","IMPRINT",FACE,{"disambiguationData":[TD([[makeQuery(id+"F4.imprint","IMPRINT",EDGE,{"disambiguationData":[TD([[subQ2,-1.0]])],"derivedFrom":subQ1}),-1.0]])]});}
            var Q24;
            {var subQ0=sQuery(id+"F4.wireOp",EDGE,"E79");var subQ1=sQuery(id+"F4.wireOp",EDGE,"E76");var subQ2=makeQuery(id+"F4.imprint","INTERSECT",VERTEX,{"derivedFrom":[subQ1,subQ0]});Q24=makeQuery(id+"F4.imprint","IMPRINT",FACE,{"disambiguationData":[TD([[makeQuery(id+"F4.imprint","IMPRINT",EDGE,{"disambiguationData":[TD([[subQ2,-1.0]])],"derivedFrom":subQ1}),-1.0]])]});}
            var Q25;
            {var subQ0=sQuery(id+"F4.wireOp",EDGE,"E79");var subQ1=sQuery(id+"F4.wireOp",EDGE,"E76");var subQ2=makeQuery(id+"F4.imprint","INTERSECT",VERTEX,{"derivedFrom":[subQ1,subQ0]});Q25=makeQuery(id+"F4.imprint","IMPRINT",FACE,{"disambiguationData":[TD([[makeQuery(id+"F4.imprint","IMPRINT",EDGE,{"disambiguationData":[TD([[subQ2,-1.0]])],"derivedFrom":subQ1}),1.0]])]});}
            var Q26;
            {var subQ0=sQuery(id+"F4.wireOp",EDGE,"E101");var subQ1=sQuery(id+"F4.wireOp",EDGE,"E76");var subQ2=makeQuery(id+"F4.imprint","INTERSECT",VERTEX,{"disambiguationData":[OD(0.0)],"derivedFrom":[subQ1,subQ0]});Q26=makeQuery(id+"F4.imprint","IMPRINT",FACE,{"disambiguationData":[TD([[makeQuery(id+"F4.imprint","IMPRINT",EDGE,{"disambiguationData":[TD([[subQ2,-1.0]])],"derivedFrom":subQ1}),1.0]])]});}
            var Q27;
            {var subQ0=sQuery(id+"F4.wireOp",EDGE,"E101");var subQ1=sQuery(id+"F4.wireOp",EDGE,"E76");var subQ2=makeQuery(id+"F4.imprint","INTERSECT",VERTEX,{"disambiguationData":[OD(0.0)],"derivedFrom":[subQ1,subQ0]});Q27=makeQuery(id+"F4.imprint","IMPRINT",FACE,{"disambiguationData":[TD([[makeQuery(id+"F4.imprint","IMPRINT",EDGE,{"disambiguationData":[TD([[subQ2,-1.0]])],"derivedFrom":subQ1}),-1.0]])]});}
            var Q28;
            {var subQ0=sQuery(id+"F4.wireOp",EDGE,"E80");var subQ1=sQuery(id+"F4.wireOp",EDGE,"E76");var subQ2=makeQuery(id+"F4.imprint","INTERSECT",VERTEX,{"derivedFrom":[subQ1,subQ0]});Q28=makeQuery(id+"F4.imprint","IMPRINT",FACE,{"disambiguationData":[TD([[makeQuery(id+"F4.imprint","IMPRINT",EDGE,{"disambiguationData":[TD([[subQ2,-1.0]])],"derivedFrom":subQ1}),-1.0]])]});}
            var Q29;
            {var subQ0=sQuery(id+"F4.wireOp",EDGE,"E80");var subQ1=sQuery(id+"F4.wireOp",EDGE,"E76");var subQ2=makeQuery(id+"F4.imprint","INTERSECT",VERTEX,{"derivedFrom":[subQ1,subQ0]});Q29=makeQuery(id+"F4.imprint","IMPRINT",FACE,{"disambiguationData":[TD([[makeQuery(id+"F4.imprint","IMPRINT",EDGE,{"disambiguationData":[TD([[subQ2,-1.0]])],"derivedFrom":subQ1}),1.0]])]});}
            var Q30;
            {var subQ0=sQuery(id+"F4.wireOp",EDGE,"E102");var subQ1=sQuery(id+"F4.wireOp",EDGE,"E76");var subQ2=makeQuery(id+"F4.imprint","INTERSECT",VERTEX,{"disambiguationData":[OD(0.0)],"derivedFrom":[subQ1,subQ0]});Q30=makeQuery(id+"F4.imprint","IMPRINT",FACE,{"disambiguationData":[TD([[makeQuery(id+"F4.imprint","IMPRINT",EDGE,{"disambiguationData":[TD([[subQ2,-1.0]])],"derivedFrom":subQ1}),1.0]])]});}
            var Q31;
            {var subQ0=sQuery(id+"F4.wireOp",EDGE,"E102");var subQ1=sQuery(id+"F4.wireOp",EDGE,"E76");var subQ2=makeQuery(id+"F4.imprint","INTERSECT",VERTEX,{"disambiguationData":[OD(0.0)],"derivedFrom":[subQ1,subQ0]});Q31=makeQuery(id+"F4.imprint","IMPRINT",FACE,{"disambiguationData":[TD([[makeQuery(id+"F4.imprint","IMPRINT",EDGE,{"disambiguationData":[TD([[subQ2,-1.0]])],"derivedFrom":subQ1}),-1.0]])]});}
            var Q32;
            {var subQ0=sQuery(id+"F4.wireOp",EDGE,"E81");var subQ1=sQuery(id+"F4.wireOp",EDGE,"E76");var subQ2=makeQuery(id+"F4.imprint","INTERSECT",VERTEX,{"derivedFrom":[subQ1,subQ0]});Q32=makeQuery(id+"F4.imprint","IMPRINT",FACE,{"disambiguationData":[TD([[makeQuery(id+"F4.imprint","IMPRINT",EDGE,{"disambiguationData":[TD([[subQ2,-1.0]])],"derivedFrom":subQ1}),-1.0]])]});}
            var Q33;
            {var subQ0=sQuery(id+"F4.wireOp",EDGE,"E81");var subQ1=sQuery(id+"F4.wireOp",EDGE,"E76");var subQ2=makeQuery(id+"F4.imprint","INTERSECT",VERTEX,{"derivedFrom":[subQ1,subQ0]});Q33=makeQuery(id+"F4.imprint","IMPRINT",FACE,{"disambiguationData":[TD([[makeQuery(id+"F4.imprint","IMPRINT",EDGE,{"disambiguationData":[TD([[subQ2,-1.0]])],"derivedFrom":subQ1}),1.0]])]});}
            var Q34;
            {var subQ0=sQuery(id+"F4.wireOp",EDGE,"E103");var subQ1=sQuery(id+"F4.wireOp",EDGE,"E76");var subQ2=makeQuery(id+"F4.imprint","INTERSECT",VERTEX,{"disambiguationData":[OD(0.0)],"derivedFrom":[subQ1,subQ0]});Q34=makeQuery(id+"F4.imprint","IMPRINT",FACE,{"disambiguationData":[TD([[makeQuery(id+"F4.imprint","IMPRINT",EDGE,{"disambiguationData":[TD([[subQ2,-1.0]])],"derivedFrom":subQ1}),1.0]])]});}
            var Q35;
            {var subQ0=sQuery(id+"F4.wireOp",EDGE,"E103");var subQ1=sQuery(id+"F4.wireOp",EDGE,"E76");var subQ2=makeQuery(id+"F4.imprint","INTERSECT",VERTEX,{"disambiguationData":[OD(0.0)],"derivedFrom":[subQ1,subQ0]});Q35=makeQuery(id+"F4.imprint","IMPRINT",FACE,{"disambiguationData":[TD([[makeQuery(id+"F4.imprint","IMPRINT",EDGE,{"disambiguationData":[TD([[subQ2,-1.0]])],"derivedFrom":subQ1}),-1.0]])]});}
            var Q36;
            {var subQ0=sQuery(id+"F4.wireOp",EDGE,"E82");var subQ1=sQuery(id+"F4.wireOp",EDGE,"E76");var subQ2=makeQuery(id+"F4.imprint","INTERSECT",VERTEX,{"derivedFrom":[subQ1,subQ0]});Q36=makeQuery(id+"F4.imprint","IMPRINT",FACE,{"disambiguationData":[TD([[makeQuery(id+"F4.imprint","IMPRINT",EDGE,{"disambiguationData":[TD([[subQ2,-1.0]])],"derivedFrom":subQ1}),-1.0]])]});}
            var Q37;
            {var subQ0=sQuery(id+"F4.wireOp",EDGE,"E82");var subQ1=sQuery(id+"F4.wireOp",EDGE,"E76");var subQ2=makeQuery(id+"F4.imprint","INTERSECT",VERTEX,{"derivedFrom":[subQ1,subQ0]});Q37=makeQuery(id+"F4.imprint","IMPRINT",FACE,{"disambiguationData":[TD([[makeQuery(id+"F4.imprint","IMPRINT",EDGE,{"disambiguationData":[TD([[subQ2,-1.0]])],"derivedFrom":subQ1}),1.0]])]});}
            var Q38;
            {var subQ0=sQuery(id+"F4.wireOp",EDGE,"E104");var subQ1=sQuery(id+"F4.wireOp",EDGE,"E76");var subQ2=makeQuery(id+"F4.imprint","INTERSECT",VERTEX,{"disambiguationData":[OD(0.0)],"derivedFrom":[subQ1,subQ0]});Q38=makeQuery(id+"F4.imprint","IMPRINT",FACE,{"disambiguationData":[TD([[makeQuery(id+"F4.imprint","IMPRINT",EDGE,{"disambiguationData":[TD([[subQ2,-1.0]])],"derivedFrom":subQ1}),1.0]])]});}
            var Q39;
            {var subQ0=sQuery(id+"F4.wireOp",EDGE,"E104");var subQ1=sQuery(id+"F4.wireOp",EDGE,"E76");var subQ2=makeQuery(id+"F4.imprint","INTERSECT",VERTEX,{"disambiguationData":[OD(0.0)],"derivedFrom":[subQ1,subQ0]});Q39=makeQuery(id+"F4.imprint","IMPRINT",FACE,{"disambiguationData":[TD([[makeQuery(id+"F4.imprint","IMPRINT",EDGE,{"disambiguationData":[TD([[subQ2,-1.0]])],"derivedFrom":subQ1}),-1.0]])]});}
            var Q40;
            {var subQ1=sQuery(id+"F4.wireOp",EDGE,"E74");var subQ3=sQuery(id+"F4.wireOp",EDGE,"E76");var subQ4=makeQuery(id+"F4.imprint","INTERSECT",VERTEX,{"derivedFrom":[subQ1,subQ3]});Q40=makeQuery(id+"F4.imprint","IMPRINT",FACE,{"disambiguationData":[TD([[makeQuery(id+"F4.imprint","IMPRINT",EDGE,{"disambiguationData":[TD([[subQ4,-1.0]])],"derivedFrom":subQ3}),-1.0]])]});}
            var Q41;
            {var subQ1=sQuery(id+"F4.wireOp",EDGE,"E74");var subQ3=sQuery(id+"F4.wireOp",EDGE,"E76");var subQ4=makeQuery(id+"F4.imprint","INTERSECT",VERTEX,{"derivedFrom":[subQ1,subQ3]});Q41=makeQuery(id+"F4.imprint","IMPRINT",FACE,{"disambiguationData":[TD([[makeQuery(id+"F4.imprint","IMPRINT",EDGE,{"disambiguationData":[TD([[subQ4,-1.0]])],"derivedFrom":subQ3}),1.0]])]});}
            var Q42;
            {var subQ1=sQuery(id+"F4.wireOp",EDGE,"E74");var subQ3=sQuery(id+"F4.wireOp",EDGE,"E76");var subQ4=makeQuery(id+"F4.imprint","INTERSECT",VERTEX,{"derivedFrom":[subQ1,subQ3]});Q42=makeQuery(id+"F4.imprint","IMPRINT",FACE,{"disambiguationData":[TD([[makeQuery(id+"F4.imprint","IMPRINT",EDGE,{"disambiguationData":[TD([[subQ4,1.0]])],"derivedFrom":subQ3}),1.0]])]});}
            var Q43;
            {var subQ1=sQuery(id+"F4.wireOp",EDGE,"E74");var subQ3=sQuery(id+"F4.wireOp",EDGE,"E76");var subQ4=makeQuery(id+"F4.imprint","INTERSECT",VERTEX,{"derivedFrom":[subQ1,subQ3]});Q43=makeQuery(id+"F4.imprint","IMPRINT",FACE,{"disambiguationData":[TD([[makeQuery(id+"F4.imprint","IMPRINT",EDGE,{"disambiguationData":[TD([[subQ4,1.0]])],"derivedFrom":subQ3}),-1.0]])]});}
            var Q44;
            {var subQ0=sQuery(id+"F4.wireOp",EDGE,"E75");var subQ1=makeQuery(id+"F4.imprint","INTERSECT",VERTEX,{"derivedFrom":[subQ0,sQuery(id+"F4.wireOp",EDGE,"E83")]});Q44=makeQuery(id+"F4.imprint","IMPRINT",FACE,{"disambiguationData":[TD([[makeQuery(id+"F4.imprint","IMPRINT",EDGE,{"disambiguationData":[TD([[subQ1,1.0]])],"derivedFrom":subQ0}),-1.0]])]});}
            var Q45;
            {var subQ0=sQuery(id+"F4.wireOp",EDGE,"E83");var subQ1=sQuery(id+"F4.wireOp",EDGE,"E75");var subQ2=makeQuery(id+"F4.imprint","INTERSECT",VERTEX,{"derivedFrom":[subQ1,subQ0]});Q45=makeQuery(id+"F4.imprint","IMPRINT",FACE,{"disambiguationData":[TD([[makeQuery(id+"F4.imprint","IMPRINT",EDGE,{"disambiguationData":[TD([[subQ2,-1.0]])],"derivedFrom":subQ0}),-1.0]])]});}
            var Q46;
            {var subQ0=sQuery(id+"F4.wireOp",EDGE,"E83");var subQ1=sQuery(id+"F4.wireOp",EDGE,"E75");var subQ2=makeQuery(id+"F4.imprint","INTERSECT",VERTEX,{"derivedFrom":[subQ1,subQ0]});Q46=makeQuery(id+"F4.imprint","IMPRINT",FACE,{"disambiguationData":[TD([[makeQuery(id+"F4.imprint","IMPRINT",EDGE,{"disambiguationData":[TD([[subQ2,-1.0]])],"derivedFrom":subQ0}),1.0]])]});}
            var Q47;
            {var subQ0=sQuery(id+"F4.wireOp",EDGE,"E83");var subQ1=sQuery(id+"F4.wireOp",EDGE,"E82");var subQ2=makeQuery(id+"F4.imprint","INTERSECT",VERTEX,{"derivedFrom":[subQ1,subQ0]});Q47=makeQuery(id+"F4.imprint","IMPRINT",FACE,{"disambiguationData":[TD([[makeQuery(id+"F4.imprint","IMPRINT",EDGE,{"disambiguationData":[TD([[subQ2,1.0]])],"derivedFrom":subQ0}),-1.0]])]});}
            var Q48;
            {var subQ0=sQuery(id+"F4.wireOp",EDGE,"E83");var subQ1=sQuery(id+"F4.wireOp",EDGE,"E82");var subQ2=makeQuery(id+"F4.imprint","INTERSECT",VERTEX,{"derivedFrom":[subQ1,subQ0]});Q48=makeQuery(id+"F4.imprint","IMPRINT",FACE,{"disambiguationData":[TD([[makeQuery(id+"F4.imprint","IMPRINT",EDGE,{"disambiguationData":[TD([[subQ2,1.0]])],"derivedFrom":subQ0}),1.0]])]});}
            var Q49;
            {var subQ0=sQuery(id+"F4.wireOp",EDGE,"E83");var subQ1=sQuery(id+"F4.wireOp",EDGE,"E82");var subQ2=makeQuery(id+"F4.imprint","INTERSECT",VERTEX,{"derivedFrom":[subQ1,subQ0]});Q49=makeQuery(id+"F4.imprint","IMPRINT",FACE,{"disambiguationData":[TD([[makeQuery(id+"F4.imprint","IMPRINT",EDGE,{"disambiguationData":[TD([[subQ2,-1.0]])],"derivedFrom":subQ0}),1.0]])]});}
            var Q50;
            {var subQ0=sQuery(id+"F4.wireOp",EDGE,"E83");var subQ1=sQuery(id+"F4.wireOp",EDGE,"E82");var subQ2=makeQuery(id+"F4.imprint","INTERSECT",VERTEX,{"derivedFrom":[subQ1,subQ0]});Q50=makeQuery(id+"F4.imprint","IMPRINT",FACE,{"disambiguationData":[TD([[makeQuery(id+"F4.imprint","IMPRINT",EDGE,{"disambiguationData":[TD([[subQ2,-1.0]])],"derivedFrom":subQ0}),-1.0]])]});}
            var Q51;
            {var subQ0=sQuery(id+"F4.wireOp",EDGE,"E83");var subQ1=sQuery(id+"F4.wireOp",EDGE,"E81");var subQ2=makeQuery(id+"F4.imprint","INTERSECT",VERTEX,{"derivedFrom":[subQ1,subQ0]});Q51=makeQuery(id+"F4.imprint","IMPRINT",FACE,{"disambiguationData":[TD([[makeQuery(id+"F4.imprint","IMPRINT",EDGE,{"disambiguationData":[TD([[subQ2,1.0]])],"derivedFrom":subQ0}),-1.0]])]});}
            var Q52;
            {var subQ0=sQuery(id+"F4.wireOp",EDGE,"E83");var subQ1=sQuery(id+"F4.wireOp",EDGE,"E81");var subQ2=makeQuery(id+"F4.imprint","INTERSECT",VERTEX,{"derivedFrom":[subQ1,subQ0]});Q52=makeQuery(id+"F4.imprint","IMPRINT",FACE,{"disambiguationData":[TD([[makeQuery(id+"F4.imprint","IMPRINT",EDGE,{"disambiguationData":[TD([[subQ2,1.0]])],"derivedFrom":subQ0}),1.0]])]});}
            var Q53;
            {var subQ0=sQuery(id+"F4.wireOp",EDGE,"E83");var subQ1=sQuery(id+"F4.wireOp",EDGE,"E81");var subQ2=makeQuery(id+"F4.imprint","INTERSECT",VERTEX,{"derivedFrom":[subQ1,subQ0]});Q53=makeQuery(id+"F4.imprint","IMPRINT",FACE,{"disambiguationData":[TD([[makeQuery(id+"F4.imprint","IMPRINT",EDGE,{"disambiguationData":[TD([[subQ2,-1.0]])],"derivedFrom":subQ0}),1.0]])]});}
            var Q54;
            {var subQ0=sQuery(id+"F4.wireOp",EDGE,"E83");var subQ1=sQuery(id+"F4.wireOp",EDGE,"E81");var subQ2=makeQuery(id+"F4.imprint","INTERSECT",VERTEX,{"derivedFrom":[subQ1,subQ0]});Q54=makeQuery(id+"F4.imprint","IMPRINT",FACE,{"disambiguationData":[TD([[makeQuery(id+"F4.imprint","IMPRINT",EDGE,{"disambiguationData":[TD([[subQ2,-1.0]])],"derivedFrom":subQ0}),-1.0]])]});}
            var Q55;
            {var subQ0=sQuery(id+"F4.wireOp",EDGE,"E83");var subQ1=sQuery(id+"F4.wireOp",EDGE,"E80");var subQ2=makeQuery(id+"F4.imprint","INTERSECT",VERTEX,{"derivedFrom":[subQ1,subQ0]});Q55=makeQuery(id+"F4.imprint","IMPRINT",FACE,{"disambiguationData":[TD([[makeQuery(id+"F4.imprint","IMPRINT",EDGE,{"disambiguationData":[TD([[subQ2,1.0]])],"derivedFrom":subQ0}),-1.0]])]});}
            var Q56;
            {var subQ0=sQuery(id+"F4.wireOp",EDGE,"E83");var subQ1=sQuery(id+"F4.wireOp",EDGE,"E80");var subQ2=makeQuery(id+"F4.imprint","INTERSECT",VERTEX,{"derivedFrom":[subQ1,subQ0]});Q56=makeQuery(id+"F4.imprint","IMPRINT",FACE,{"disambiguationData":[TD([[makeQuery(id+"F4.imprint","IMPRINT",EDGE,{"disambiguationData":[TD([[subQ2,1.0]])],"derivedFrom":subQ0}),1.0]])]});}
            var Q57;
            {var subQ0=sQuery(id+"F4.wireOp",EDGE,"E83");var subQ1=sQuery(id+"F4.wireOp",EDGE,"E80");var subQ2=makeQuery(id+"F4.imprint","INTERSECT",VERTEX,{"derivedFrom":[subQ1,subQ0]});Q57=makeQuery(id+"F4.imprint","IMPRINT",FACE,{"disambiguationData":[TD([[makeQuery(id+"F4.imprint","IMPRINT",EDGE,{"disambiguationData":[TD([[subQ2,-1.0]])],"derivedFrom":subQ0}),1.0]])]});}
            var Q58;
            {var subQ0=sQuery(id+"F4.wireOp",EDGE,"E83");var subQ1=sQuery(id+"F4.wireOp",EDGE,"E80");var subQ2=makeQuery(id+"F4.imprint","INTERSECT",VERTEX,{"derivedFrom":[subQ1,subQ0]});Q58=makeQuery(id+"F4.imprint","IMPRINT",FACE,{"disambiguationData":[TD([[makeQuery(id+"F4.imprint","IMPRINT",EDGE,{"disambiguationData":[TD([[subQ2,-1.0]])],"derivedFrom":subQ0}),-1.0]])]});}
            var Q59;
            {var subQ0=sQuery(id+"F4.wireOp",EDGE,"E83");var subQ1=sQuery(id+"F4.wireOp",EDGE,"E79");var subQ2=makeQuery(id+"F4.imprint","INTERSECT",VERTEX,{"derivedFrom":[subQ1,subQ0]});Q59=makeQuery(id+"F4.imprint","IMPRINT",FACE,{"disambiguationData":[TD([[makeQuery(id+"F4.imprint","IMPRINT",EDGE,{"disambiguationData":[TD([[subQ2,1.0]])],"derivedFrom":subQ0}),-1.0]])]});}
            var Q60;
            {var subQ0=sQuery(id+"F4.wireOp",EDGE,"E83");var subQ1=sQuery(id+"F4.wireOp",EDGE,"E79");var subQ2=makeQuery(id+"F4.imprint","INTERSECT",VERTEX,{"derivedFrom":[subQ1,subQ0]});Q60=makeQuery(id+"F4.imprint","IMPRINT",FACE,{"disambiguationData":[TD([[makeQuery(id+"F4.imprint","IMPRINT",EDGE,{"disambiguationData":[TD([[subQ2,1.0]])],"derivedFrom":subQ0}),1.0]])]});}
            var Q61;
            {var subQ0=sQuery(id+"F4.wireOp",EDGE,"E83");var subQ1=sQuery(id+"F4.wireOp",EDGE,"E79");var subQ2=makeQuery(id+"F4.imprint","INTERSECT",VERTEX,{"derivedFrom":[subQ1,subQ0]});Q61=makeQuery(id+"F4.imprint","IMPRINT",FACE,{"disambiguationData":[TD([[makeQuery(id+"F4.imprint","IMPRINT",EDGE,{"disambiguationData":[TD([[subQ2,-1.0]])],"derivedFrom":subQ0}),1.0]])]});}
            var Q62;
            {var subQ0=sQuery(id+"F4.wireOp",EDGE,"E83");var subQ1=sQuery(id+"F4.wireOp",EDGE,"E79");var subQ2=makeQuery(id+"F4.imprint","INTERSECT",VERTEX,{"derivedFrom":[subQ1,subQ0]});Q62=makeQuery(id+"F4.imprint","IMPRINT",FACE,{"disambiguationData":[TD([[makeQuery(id+"F4.imprint","IMPRINT",EDGE,{"disambiguationData":[TD([[subQ2,-1.0]])],"derivedFrom":subQ0}),-1.0]])]});}
            var Q63;
            {var subQ0=sQuery(id+"F4.wireOp",EDGE,"E83");var subQ1=sQuery(id+"F4.wireOp",EDGE,"E78");var subQ2=makeQuery(id+"F4.imprint","INTERSECT",VERTEX,{"derivedFrom":[subQ1,subQ0]});Q63=makeQuery(id+"F4.imprint","IMPRINT",FACE,{"disambiguationData":[TD([[makeQuery(id+"F4.imprint","IMPRINT",EDGE,{"disambiguationData":[TD([[subQ2,1.0]])],"derivedFrom":subQ0}),-1.0]])]});}
            var Q64;
            {var subQ0=sQuery(id+"F4.wireOp",EDGE,"E83");var subQ1=sQuery(id+"F4.wireOp",EDGE,"E78");var subQ2=makeQuery(id+"F4.imprint","INTERSECT",VERTEX,{"derivedFrom":[subQ1,subQ0]});Q64=makeQuery(id+"F4.imprint","IMPRINT",FACE,{"disambiguationData":[TD([[makeQuery(id+"F4.imprint","IMPRINT",EDGE,{"disambiguationData":[TD([[subQ2,1.0]])],"derivedFrom":subQ0}),1.0]])]});}
            var Q65;
            {var subQ0=sQuery(id+"F4.wireOp",EDGE,"E83");var subQ1=sQuery(id+"F4.wireOp",EDGE,"E78");var subQ2=makeQuery(id+"F4.imprint","INTERSECT",VERTEX,{"derivedFrom":[subQ1,subQ0]});Q65=makeQuery(id+"F4.imprint","IMPRINT",FACE,{"disambiguationData":[TD([[makeQuery(id+"F4.imprint","IMPRINT",EDGE,{"disambiguationData":[TD([[subQ2,-1.0]])],"derivedFrom":subQ0}),1.0]])]});}
            var Q66;
            {var subQ0=sQuery(id+"F4.wireOp",EDGE,"E83");var subQ1=sQuery(id+"F4.wireOp",EDGE,"E78");var subQ2=makeQuery(id+"F4.imprint","INTERSECT",VERTEX,{"derivedFrom":[subQ1,subQ0]});Q66=makeQuery(id+"F4.imprint","IMPRINT",FACE,{"disambiguationData":[TD([[makeQuery(id+"F4.imprint","IMPRINT",EDGE,{"disambiguationData":[TD([[subQ2,-1.0]])],"derivedFrom":subQ0}),-1.0]])]});}
            var Q67;
            {var subQ0=sQuery(id+"F4.wireOp",EDGE,"E83");var subQ1=sQuery(id+"F4.wireOp",EDGE,"E77");var subQ2=makeQuery(id+"F4.imprint","INTERSECT",VERTEX,{"derivedFrom":[subQ1,subQ0]});Q67=makeQuery(id+"F4.imprint","IMPRINT",FACE,{"disambiguationData":[TD([[makeQuery(id+"F4.imprint","IMPRINT",EDGE,{"disambiguationData":[TD([[subQ2,1.0]])],"derivedFrom":subQ0}),-1.0]])]});}
            var Q68;
            {var subQ0=sQuery(id+"F4.wireOp",EDGE,"E83");var subQ1=sQuery(id+"F4.wireOp",EDGE,"E77");var subQ2=makeQuery(id+"F4.imprint","INTERSECT",VERTEX,{"derivedFrom":[subQ1,subQ0]});Q68=makeQuery(id+"F4.imprint","IMPRINT",FACE,{"disambiguationData":[TD([[makeQuery(id+"F4.imprint","IMPRINT",EDGE,{"disambiguationData":[TD([[subQ2,1.0]])],"derivedFrom":subQ0}),1.0]])]});}
            var Q69;
            {var subQ0=sQuery(id+"F4.wireOp",EDGE,"E83");var subQ1=sQuery(id+"F4.wireOp",EDGE,"E77");var subQ2=makeQuery(id+"F4.imprint","INTERSECT",VERTEX,{"derivedFrom":[subQ1,subQ0]});Q69=makeQuery(id+"F4.imprint","IMPRINT",FACE,{"disambiguationData":[TD([[makeQuery(id+"F4.imprint","IMPRINT",EDGE,{"disambiguationData":[TD([[subQ2,-1.0]])],"derivedFrom":subQ0}),1.0]])]});}
            var Q70;
            {var subQ0=sQuery(id+"F4.wireOp",EDGE,"E83");var subQ1=sQuery(id+"F4.wireOp",EDGE,"E77");var subQ2=makeQuery(id+"F4.imprint","INTERSECT",VERTEX,{"derivedFrom":[subQ1,subQ0]});Q70=makeQuery(id+"F4.imprint","IMPRINT",FACE,{"disambiguationData":[TD([[makeQuery(id+"F4.imprint","IMPRINT",EDGE,{"disambiguationData":[TD([[subQ2,-1.0]])],"derivedFrom":subQ0}),-1.0]])]});}
            var Q71;
            {var subQ0=sQuery(id+"F4.wireOp",EDGE,"E77");var subQ1=sQuery(id+"F4.wireOp",EDGE,"E76");var subQ2=makeQuery(id+"F4.imprint","INTERSECT",VERTEX,{"derivedFrom":[subQ1,subQ0]});Q71=makeQuery(id+"F4.imprint","IMPRINT",FACE,{"disambiguationData":[TD([[makeQuery(id+"F4.imprint","IMPRINT",EDGE,{"disambiguationData":[TD([[subQ2,-1.0]])],"derivedFrom":subQ1}),1.0]])]});}
            var Q72;
            {var subQ0=sQuery(id+"F4.wireOp",EDGE,"E99");var subQ1=sQuery(id+"F4.wireOp",EDGE,"E76");var subQ2=makeQuery(id+"F4.imprint","INTERSECT",VERTEX,{"disambiguationData":[OD(0.0)],"derivedFrom":[subQ1,subQ0]});Q72=makeQuery(id+"F4.imprint","IMPRINT",FACE,{"disambiguationData":[TD([[makeQuery(id+"F4.imprint","IMPRINT",EDGE,{"disambiguationData":[TD([[subQ2,-1.0]])],"derivedFrom":subQ1}),1.0]])]});}
            var Q73;
            {var subQ0=sQuery(id+"F4.wireOp",EDGE,"E99");var subQ1=sQuery(id+"F4.wireOp",EDGE,"E76");var subQ2=makeQuery(id+"F4.imprint","INTERSECT",VERTEX,{"disambiguationData":[OD(0.0)],"derivedFrom":[subQ1,subQ0]});Q73=makeQuery(id+"F4.imprint","IMPRINT",FACE,{"disambiguationData":[TD([[makeQuery(id+"F4.imprint","IMPRINT",EDGE,{"disambiguationData":[TD([[subQ2,-1.0]])],"derivedFrom":subQ1}),-1.0]])]});}
            var Q74;
            {var subQ0=sQuery(id+"F4.wireOp",EDGE,"E77");var subQ1=sQuery(id+"F4.wireOp",EDGE,"E76");var subQ2=makeQuery(id+"F4.imprint","INTERSECT",VERTEX,{"derivedFrom":[subQ1,subQ0]});Q74=makeQuery(id+"F4.imprint","IMPRINT",FACE,{"disambiguationData":[TD([[makeQuery(id+"F4.imprint","IMPRINT",EDGE,{"disambiguationData":[TD([[subQ2,-1.0]])],"derivedFrom":subQ1}),-1.0]])]});}
            var Q75;
            {var subQ0=sQuery(id+"F4.wireOp",EDGE,"E77");var subQ1=sQuery(id+"F4.wireOp",EDGE,"E71");var subQ2=makeQuery(id+"F4.imprint","INTERSECT",VERTEX,{"derivedFrom":[subQ1,subQ0]});Q75=makeQuery(id+"F4.imprint","IMPRINT",FACE,{"disambiguationData":[TD([[makeQuery(id+"F4.imprint","IMPRINT",EDGE,{"disambiguationData":[TD([[subQ2,-1.0]])],"derivedFrom":subQ1}),1.0]])]});}
            var Q76;
            {var subQ0=sQuery(id+"F4.wireOp",EDGE,"E89");var subQ1=sQuery(id+"F4.wireOp",EDGE,"E71");var subQ2=makeQuery(id+"F4.imprint","INTERSECT",VERTEX,{"disambiguationData":[OD(0.0)],"derivedFrom":[subQ1,subQ0]});Q76=makeQuery(id+"F4.imprint","IMPRINT",FACE,{"disambiguationData":[TD([[makeQuery(id+"F4.imprint","IMPRINT",EDGE,{"disambiguationData":[TD([[subQ2,-1.0]])],"derivedFrom":subQ1}),1.0]])]});}
            var Q77;
            {var subQ0=sQuery(id+"F4.wireOp",EDGE,"E89");var subQ1=sQuery(id+"F4.wireOp",EDGE,"E71");var subQ2=makeQuery(id+"F4.imprint","INTERSECT",VERTEX,{"disambiguationData":[OD(0.0)],"derivedFrom":[subQ1,subQ0]});Q77=makeQuery(id+"F4.imprint","IMPRINT",FACE,{"disambiguationData":[TD([[makeQuery(id+"F4.imprint","IMPRINT",EDGE,{"disambiguationData":[TD([[subQ2,-1.0]])],"derivedFrom":subQ1}),-1.0]])]});}
            var Q78;
            {var subQ0=sQuery(id+"F4.wireOp",EDGE,"E77");var subQ1=sQuery(id+"F4.wireOp",EDGE,"E71");var subQ2=makeQuery(id+"F4.imprint","INTERSECT",VERTEX,{"derivedFrom":[subQ1,subQ0]});Q78=makeQuery(id+"F4.imprint","IMPRINT",FACE,{"disambiguationData":[TD([[makeQuery(id+"F4.imprint","IMPRINT",EDGE,{"disambiguationData":[TD([[subQ2,-1.0]])],"derivedFrom":subQ1}),-1.0]])]});}
            extrude(context, id + "F10", {"entities" : qUnion([Q0, Q1, Q2, Q3, Q4, Q5, Q6, Q7, Q8, Q9, Q10, Q11, Q12, Q13, Q14, Q15, Q16, Q17, Q18, Q19, Q20, Q21, Q22, Q23, Q24, Q25, Q26, Q27, Q28, Q29, Q30, Q31, Q32, Q33, Q34, Q35, Q36, Q37, Q38, Q39, Q40, Q41, Q42, Q43, Q44, Q45, Q46, Q47, Q48, Q49, Q50, Q51, Q52, Q53, Q54, Q55, Q56, Q57, Q58, Q59, Q60, Q61, Q62, Q63, Q64, Q65, Q66, Q67, Q68, Q69, Q70, Q71, Q72, Q73, Q74, Q75, Q76, Q77, Q78]), "operationType" : NewBodyOperationType.ADD, "depth" : 2.5 * mm});
        }
        {
            var Q0;
            Q0=makeQuery(id+"F7.opExtrude","CAP_FACE",FACE,{"disambiguationData":[OSD([sQuery(id+"F4.wireOp",EDGE,"E48"),sQuery(id+"F4.wireOp",EDGE,"E60")])],"isStart":false});
            extrude(context, id + "F11", {"entities" : qUnion([Q0]), "operationType" : NewBodyOperationType.ADD, "depth" : 2.5 * mm});
        }
    });
